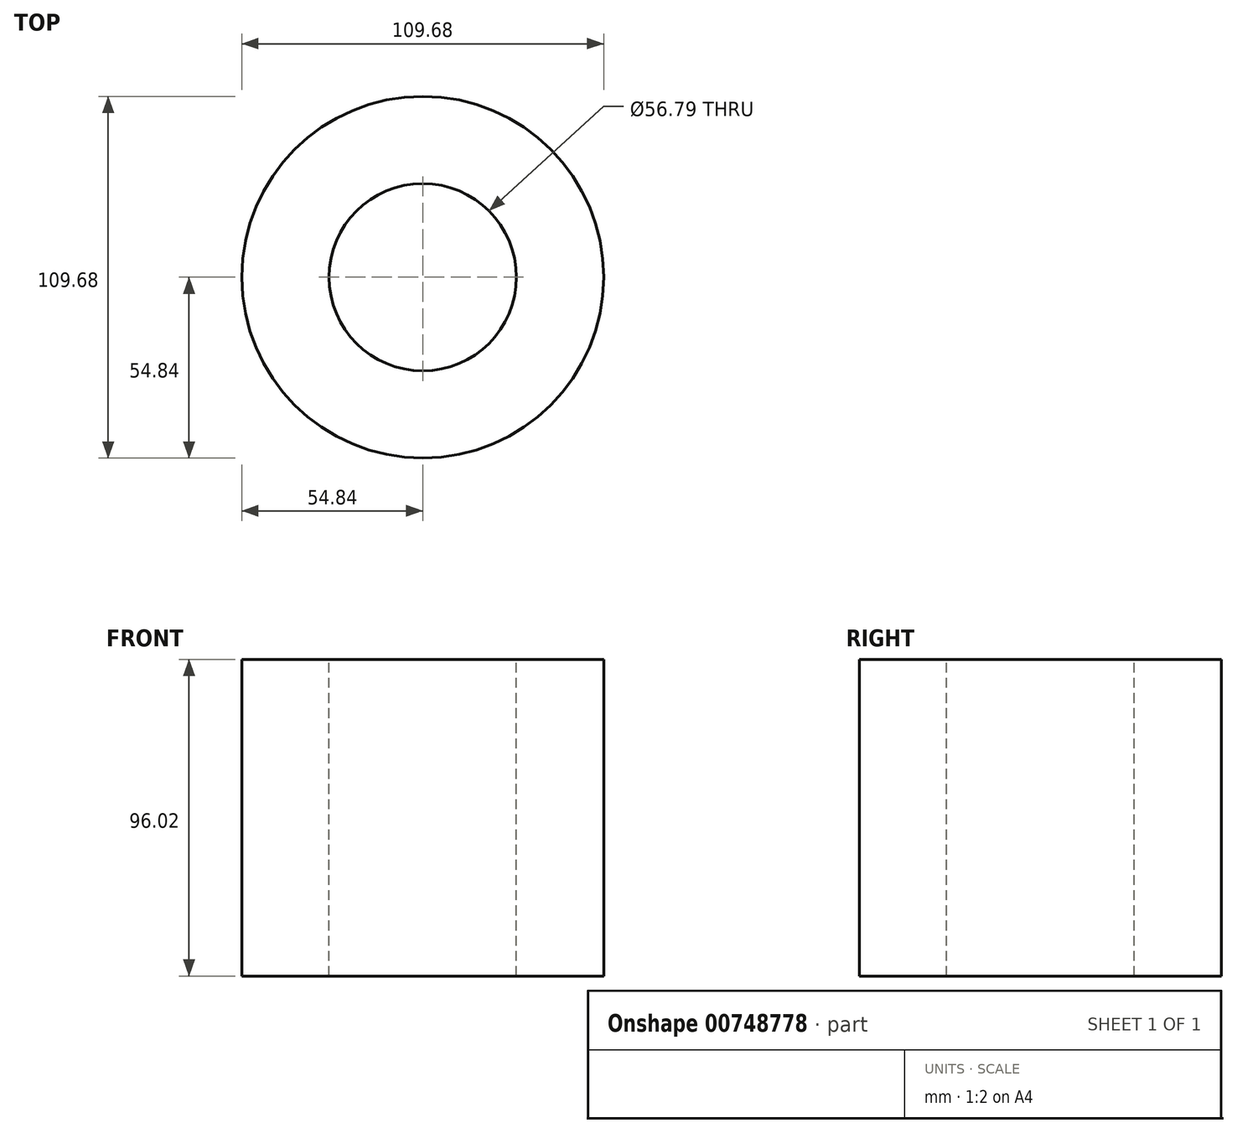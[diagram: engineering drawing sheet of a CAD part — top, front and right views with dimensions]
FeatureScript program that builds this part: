
annotation { "Feature Type Name" : "Feature", "Feature Type Description" : "" }
export const myFeature = defineFeature(function(context is Context, id is Id, definition is map)
    precondition{}
    {
        {
            var Q0;
            Q0=qCreatedBy(makeId("Top.planeOp"),FACE);
            var sketch = newSketch(context, id + "F0", { "sketchPlane" : qUnion([Q0])});
            skCircle(sketch, "E0", {"center": v(0, 0) * mm, "radius": 54.84 * mm});
            skSolve(sketch);
        }
        {
            var Q0;
            Q0 = qSketchRegion(id + "F0", true);
            extrude(context, id + "F1", {"entities" : qUnion([Q0]), "endBound" : BoundingType.SYMMETRIC, "depth" : 96.01 * mm, "offsetDistance" : 25.4 * mm});
        }
        {
            var Q0;
            Q0=makeQuery(id+"F1.opExtrude","CAP_FACE",FACE,{"disambiguationData":[OSD([sQuery(id+"F0.wireOp",EDGE,"E0")])],"isStart":false});
            var sketch = newSketch(context, id + "F2", { "sketchPlane" : qUnion([Q0])});
            skCircle(sketch, "E1", {"center": v(0, 0) * mm, "radius": 26.96 * mm});
            skSolve(sketch);
        }
        {
            var Q0;
            Q0 = qSketchRegion(id + "F2", true);
            extrude(context, id + "F3", {"entities" : qUnion([Q0]), "operationType" : NewBodyOperationType.ADD, "oppositeDirection" : true, "depth" : 75.95 * mm, "offsetDistance" : 25.4 * mm});
        }
        {
            var Q0;
            Q0=makeQuery(id+"F1.opExtrude","CAP_FACE",FACE,{"disambiguationData":[OSD([sQuery(id+"F0.wireOp",EDGE,"E0")])],"isStart":false});
            var sketch = newSketch(context, id + "F4", { "sketchPlane" : qUnion([Q0])});
            skCircle(sketch, "E2", {"center": v(0, 0) * mm, "radius": 28.4 * mm});
            skSolve(sketch);
        }
        {
            var Q0;
            Q0 = qSketchRegion(id + "F4", true);
            var Q1;
            Q1=makeQuery(id+"F4.imprint","IMPRINT",FACE,{"disambiguationData":[TD([[makeQuery(id+"F4.imprint","IMPRINT",EDGE,{"derivedFrom":sQuery(id+"F4.wireOp",EDGE,"E2")}),1.0]])]});
            extrude(context, id + "F5", {"entities" : qUnion([Q0, Q1]), "operationType" : NewBodyOperationType.REMOVE, "oppositeDirection" : true, "depth" : 97.03 * mm, "offsetDistance" : 25.4 * mm});
        }
    });
